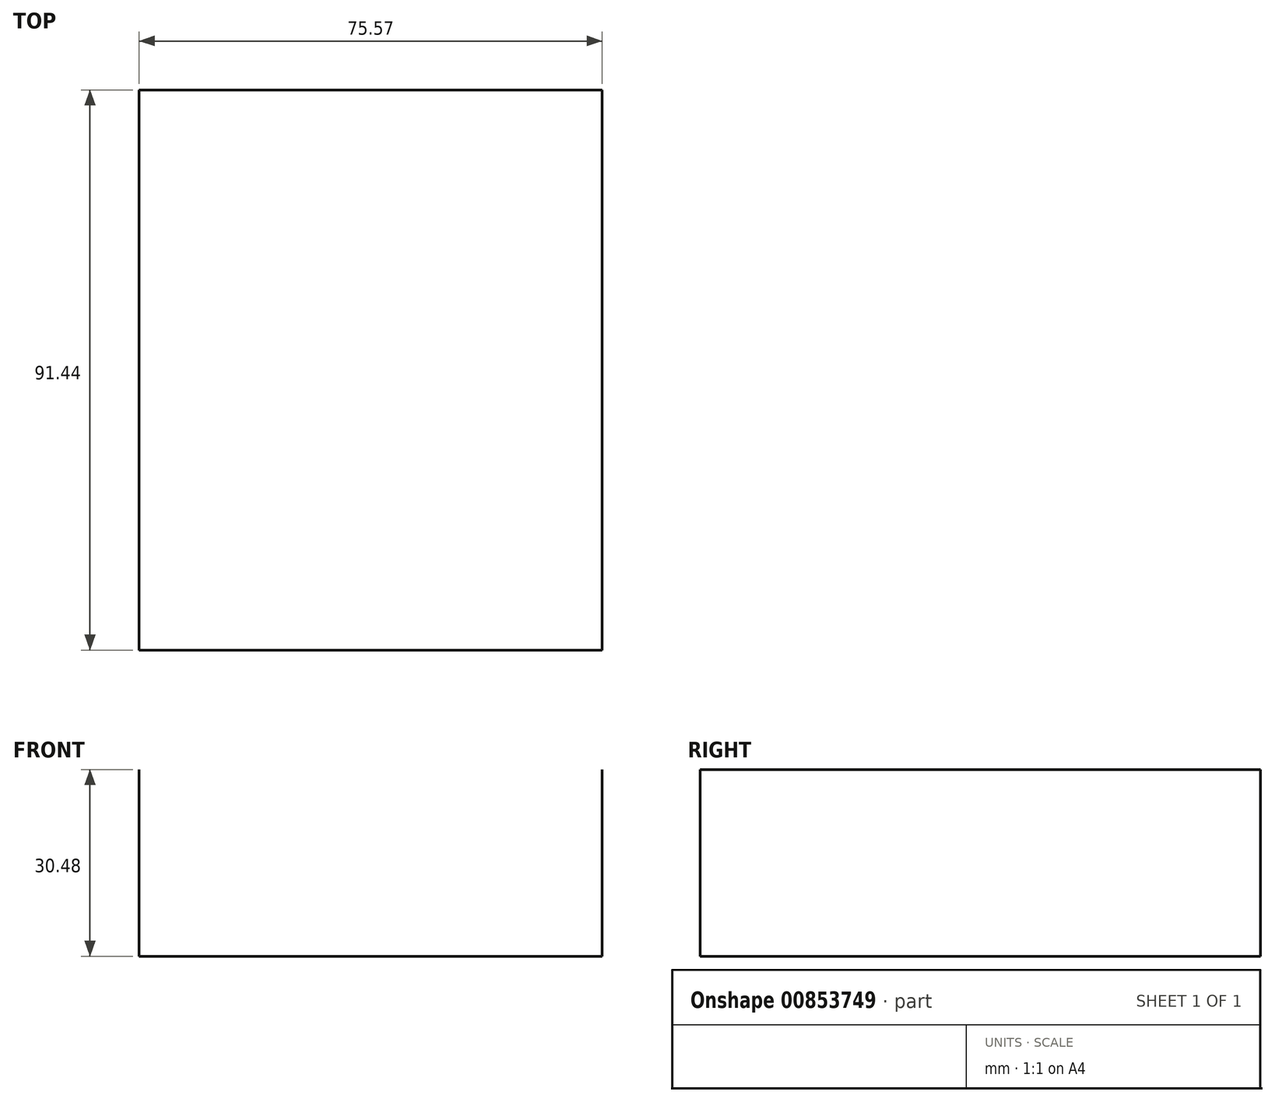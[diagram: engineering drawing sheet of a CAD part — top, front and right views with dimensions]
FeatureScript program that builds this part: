
annotation { "Feature Type Name" : "Feature", "Feature Type Description" : "" }
export const myFeature = defineFeature(function(context is Context, id is Id, definition is map)
    precondition{}
    {
        {
            var Q0;
            Q0=qCreatedBy(makeId("Front.planeOp"),FACE);
            var sketch = newSketch(context, id + "F0", { "sketchPlane" : qUnion([Q0])});
            skLineSegment(sketch, "E0", {"start": v(0, 0) * mm, "end": v(0, -30.48) * mm});
            skLineSegment(sketch, "E1", {"start": v(0, -30.48) * mm, "end": v(75.57, -30.48) * mm});
            skLineSegment(sketch, "E2", {"start": v(75.57, -30.48) * mm, "end": v(75.57, 0) * mm});
            skSolve(sketch);
        }
        {
            var Q0;
            Q0=sQuery(id+"F0.wireOp",EDGE,"E0");
            var Q1;
            Q1=sQuery(id+"F0.wireOp",EDGE,"E1");
            var Q2;
            Q2=sQuery(id+"F0.wireOp",EDGE,"E2");
            extrude(context, id + "F1", {"bodyType" : ToolBodyType.SURFACE, "operationType" : NewBodyOperationType.ADD, "surfaceEntities" : qUnion([Q0, Q1, Q2]), "depth" : 91.44 * mm, "offsetDistance" : 30.48 * mm});
        }
    });
